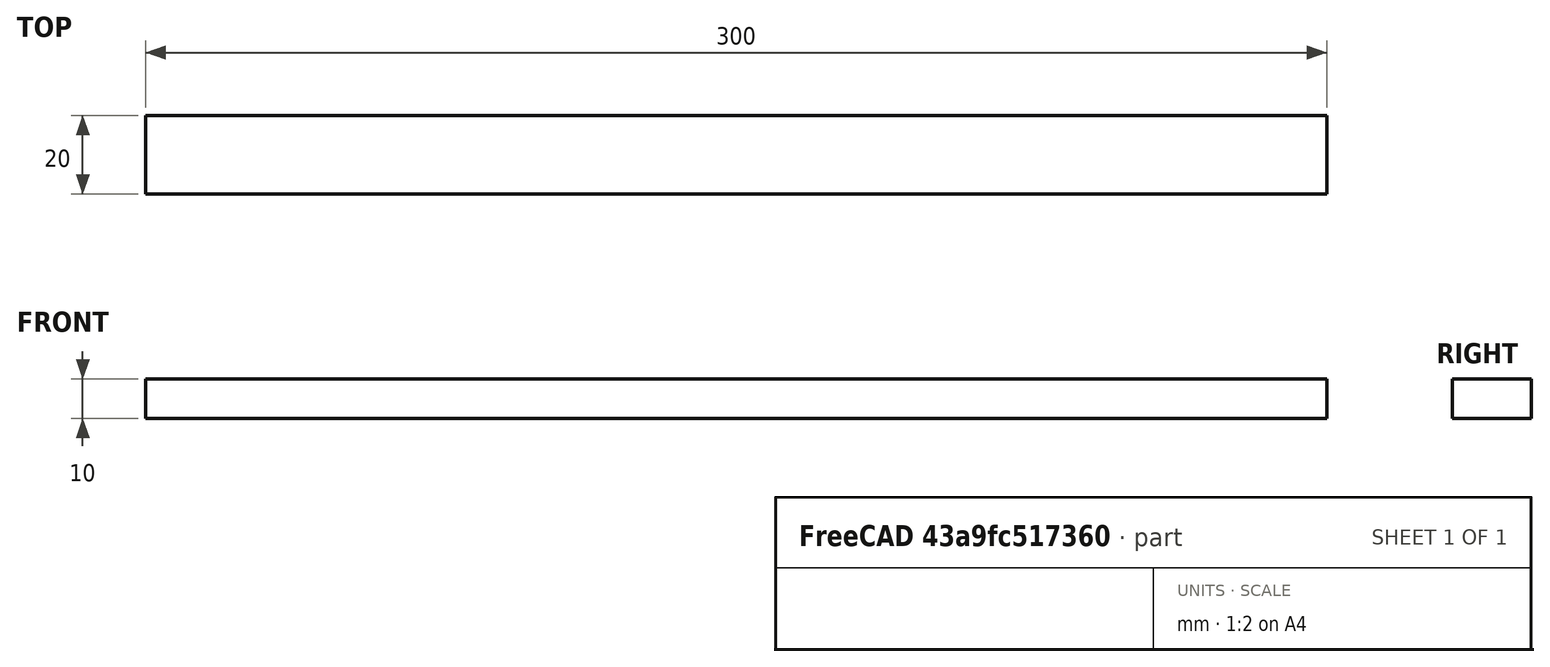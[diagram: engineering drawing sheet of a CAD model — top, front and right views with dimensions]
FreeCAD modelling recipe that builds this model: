
FCSTD DOCUMENT  (FreeCAD 0.20R29410 (Git))
Label: Bar_Plus50mm
License: All rights reserved
LicenseURL: http://en.wikipedia.org/wiki/All_rights_reserved
objects: Sketcher::SketchObject×1, PartDesign::Pad×1, PartDesign::Body×1
note: 4 computed .brp shape members not serialized (recipe doc carries the construction recipe); baked Part::Feature solids carry a one-line shape summary decoded from their .brp

FEATURE [Sketcher::SketchObject] Sketch
  FullyConstrained = true
  MapMode = 5
  Placement = pos=(0,0,0) rot=(0.57735,0.57735,0.57735;2.0944rad)
  Support = -> [YZ_Plane]
  sketch-geometry (5):
    g0: LineSegment StartX=-40 StartY=5 StartZ=0 EndX=-40 EndY=-5 EndZ=0
    g1: LineSegment StartX=-40 StartY=-5 StartZ=0 EndX=-60 EndY=-5 EndZ=0
    g2: LineSegment StartX=-60 StartY=-5 StartZ=0 EndX=-60 EndY=5 EndZ=0
    g3: LineSegment StartX=-60 StartY=5 StartZ=0 EndX=-40 EndY=5 EndZ=0
    g4: GeomPoint X=-50 Y=-1e-16 Z=0
  constraints (13):
    c: Coincident(g0,g1)
    c: Coincident(g1,g2)
    c: Coincident(g2,g3)
    c: Coincident(g3,g0)
    c: Horizontal(g1)
    c: Horizontal(g3)
    c: Vertical(g0)
    c: Vertical(g2)
    c: Symmetric(g1,g0,g4)
    c: DistanceY(g-1,g4) = 0
    c: DistanceX(g4,g-1) = 50
    c: DistanceX(g1,g1) = 20
    c: DistanceY(g2,g2) = 10
FEATURE [PartDesign::Pad] Pad
  Direction = (1,-2e-16,3e-16)
  Length = 300
  Length2 = 10
  Placement = pos=(0,0,0) rot=(0.57735,0.57735,0.57735;2.0944rad)
  Profile = -> Sketch
  ReferenceAxis = -> Sketch [N_Axis]
  Type = 0
FEATURE [PartDesign::Body] Body
  Group = -> [Sketch,Pad]
  Origin = -> Origin
  Tip = -> Pad
